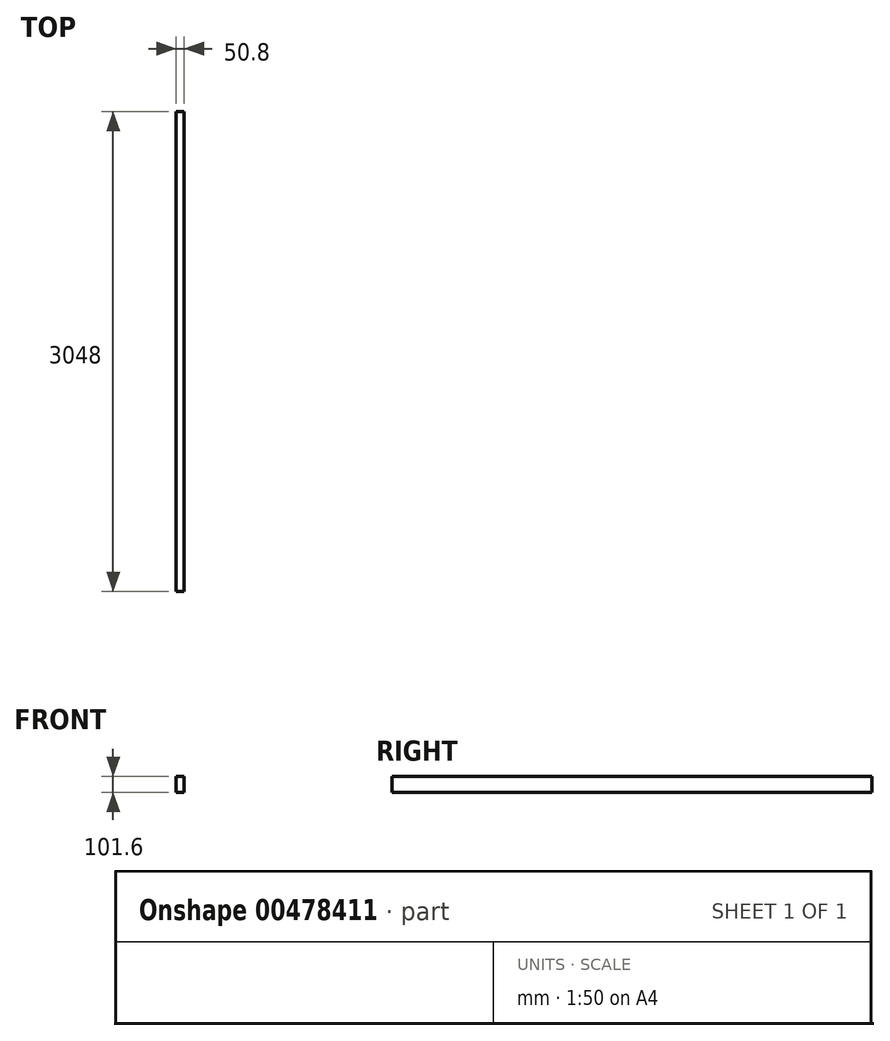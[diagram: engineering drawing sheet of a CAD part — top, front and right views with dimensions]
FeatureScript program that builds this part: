
annotation { "Feature Type Name" : "Feature", "Feature Type Description" : "" }
export const myFeature = defineFeature(function(context is Context, id is Id, definition is map)
    precondition{}
    {
        {
            var Q0;
            Q0=qCreatedBy(makeId("Front.planeOp"),FACE);
            var sketch = newSketch(context, id + "F0", { "sketchPlane" : qUnion([Q0])});
            skLineSegment(sketch, "E0.bottom", {"start": v(-22.27, 96.12) * mm, "end": v(28.53, 96.12) * mm});
            skLineSegment(sketch, "E0.top", {"start": v(-22.27, -5.48) * mm, "end": v(28.53, -5.48) * mm});
            skLineSegment(sketch, "E0.left", {"start": v(-22.27, 96.12) * mm, "end": v(-22.27, -5.48) * mm});
            skLineSegment(sketch, "E0.right", {"start": v(28.53, 96.12) * mm, "end": v(28.53, -5.48) * mm});
            skSolve(sketch);
        }
        {
            var Q0;
            Q0=makeQuery(id+"F0.imprint","IMPRINT",FACE,{"disambiguationData":[TD([[makeQuery(id+"F0.imprint","IMPRINT",EDGE,{"derivedFrom":sQuery(id+"F0.wireOp",EDGE,"E0.bottom")}),-1.0]])]});
            extrude(context, id + "F1", {"entities" : qUnion([Q0]), "depth" : 3048 * mm});
        }
    });
